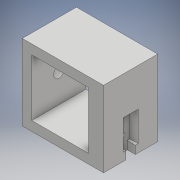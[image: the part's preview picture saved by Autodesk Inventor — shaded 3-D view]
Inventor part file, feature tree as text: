
AUTODESK INVENTOR PART (.ipt)
format: ipt  version: 2017 (Build 210142000, 142)  size: 139,776 bytes
history: native  units: mm
features: extrude x4, sketch x4
ambient origin geometry x8: Origin, YZ Plane, XZ Plane, XY Plane, X Axis, Y Axis, Z Axis, Center Point
bodies: Solid1 (feature_tree)
feature tree (8):
  extrude  "Extrusion1"  Depth=21.0mm
  extrude  "Extrusion2"  Depth=28.0mm
  extrude  "Extrusion3"  Depth=20.0mm
  extrude  "Extrusion4"  Depth=1.0mm
  sketch  "Sketch1"  dims[d0=21.0mm d1=21.0mm]
  sketch  "Sketch3"  dims[d2=28.0mm d3=28.0mm]
  sketch  "Sketch4"  dims[d4=20.0mm d5=0.0mm d6=2.0mm]
  sketch  "Sketch5"  dims[d7=2.75mm d8=2.75mm d9=1.0mm d10=3.0mm d11=1.0mm d12=3.0mm d13=0.0mm d14=1.9mm d15=1.9mm d16=6.0mm d17=3.0mm d18=0.0mm d19=3.9mm d20=4.0mm d21=0.0mm d22=2.5mm d23=1.0mm]
